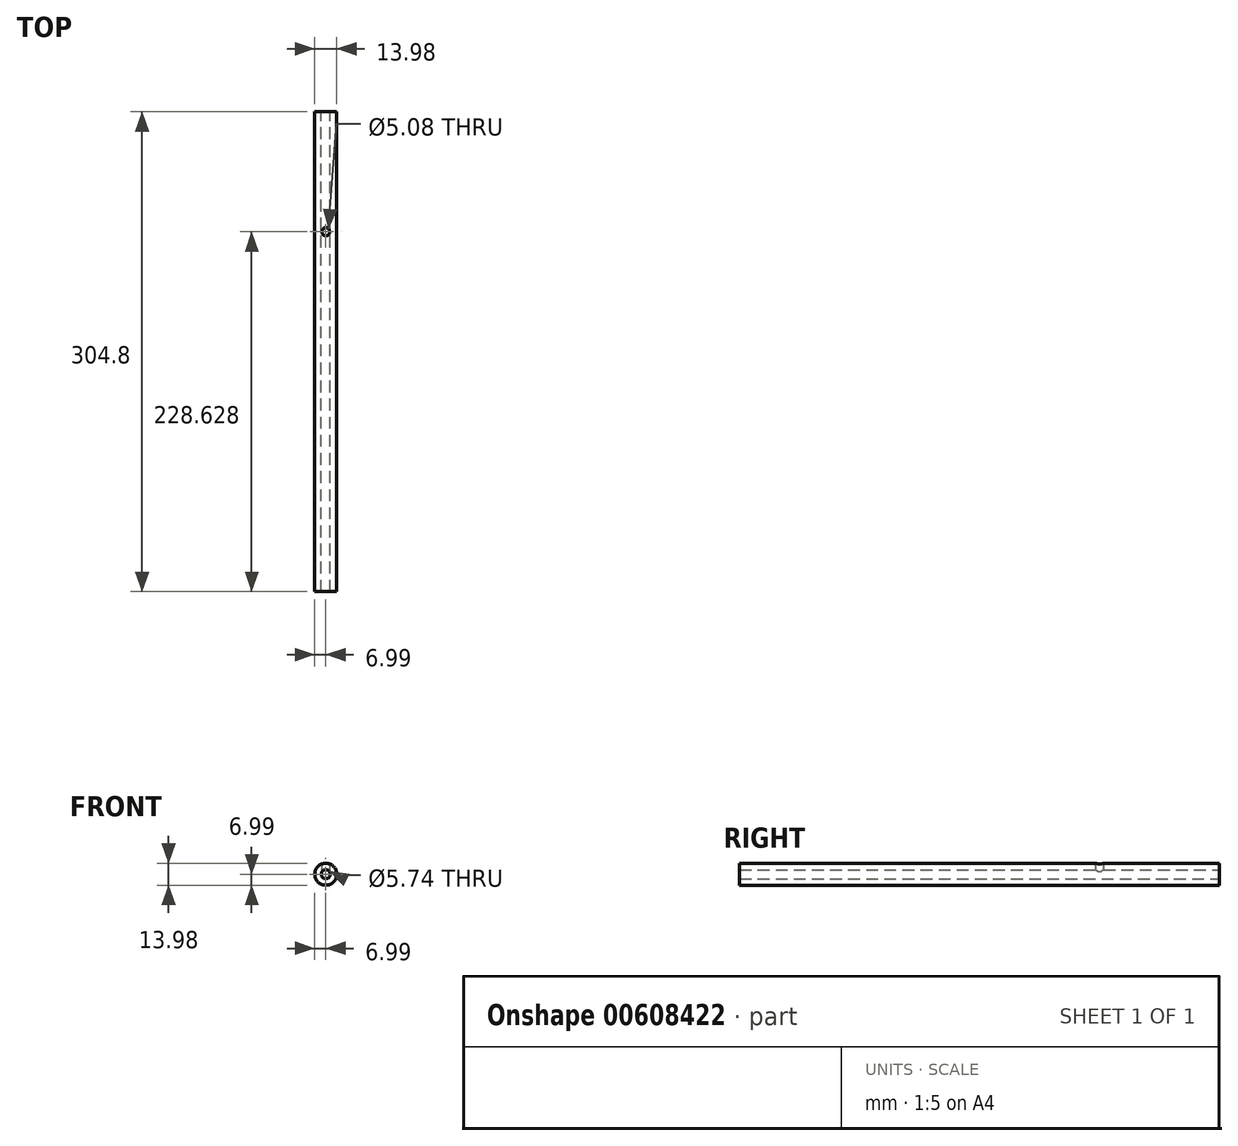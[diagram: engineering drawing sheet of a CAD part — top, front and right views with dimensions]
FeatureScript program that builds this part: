
annotation { "Feature Type Name" : "Feature", "Feature Type Description" : "" }
export const myFeature = defineFeature(function(context is Context, id is Id, definition is map)
    precondition{}
    {
        {
            var Q0;
            Q0=qCreatedBy(makeId("Front.planeOp"),FACE);
            var sketch = newSketch(context, id + "F0", { "sketchPlane" : qUnion([Q0])});
            skCircle(sketch, "E0", {"center": v(0, 0) * mm, "radius": 6.99 * mm});
            skSolve(sketch);
        }
        {
            var Q0;
            Q0=makeQuery(id+"F0.imprint","IMPRINT",FACE,{"disambiguationData":[TD([[makeQuery(id+"F0.imprint","IMPRINT",EDGE,{"derivedFrom":sQuery(id+"F0.wireOp",EDGE,"E0")}),1.0]])]});
            extrude(context, id + "F1", {"entities" : qUnion([Q0]), "depth" : 304.8 * mm, "offsetDistance" : 25.4 * mm});
        }
        {
            var Q0;
            Q0=qCreatedBy(makeId("Front.planeOp"),FACE);
            var sketch = newSketch(context, id + "F2", { "sketchPlane" : qUnion([Q0])});
            skPoint(sketch, "E1", {"position": v(0, 0) * mm});
            skSolve(sketch);
        }
        {
            var Q0;
            Q0=sQuery(id+"F2.wireOp",VERTEX,"E1");
            var Q1;
            Q1=makeQuery(id+"F1.opExtrude","SWEPT_BODY",BODY,{"disambiguationData":[OSD([sQuery(id+"F0.wireOp",EDGE,"E0")])]});
            hole(context, id + "F3", {"style" : HoleStyle.SIMPLE, "endStyle" : HoleEndStyle.BLIND, "oppositeDirection" : true, "holeDiameter" : 5.74 * mm, "majorDiameter" : 6.35 * mm, "holeDepth" : 304.8 * mm, "isTappedThrough" : true, "tappedDepth" : 12.7 * mm, "tapClearance" : 3, "startFromSketch" : true, "locations" : qUnion([Q0]), "scope" : qUnion([Q1])});
        }
        {
            var Q0;
            Q0=qCreatedBy(makeId("Top.planeOp"),FACE);
            var sketch = newSketch(context, id + "F4", { "sketchPlane" : qUnion([Q0])});
            skPoint(sketch, "E2", {"position": v(0, -76.17) * mm});
            skSolve(sketch);
        }
        {
            var Q0;
            Q0=sQuery(id+"F4.wireOp",VERTEX,"E2");
            var Q1;
            Q1=makeQuery(id+"F1.opExtrude","SWEPT_BODY",BODY,{"disambiguationData":[OSD([sQuery(id+"F0.wireOp",EDGE,"E0")])]});
            hole(context, id + "F5", {"style" : HoleStyle.SIMPLE, "endStyle" : HoleEndStyle.BLIND, "oppositeDirection" : true, "holeDiameter" : 5.08 * mm, "majorDiameter" : 6.35 * mm, "holeDepth" : 25.4 * mm, "isTappedThrough" : true, "tappedDepth" : 12.7 * mm, "tapClearance" : 3, "startFromSketch" : true, "locations" : qUnion([Q0]), "scope" : qUnion([Q1])});
        }
    });
